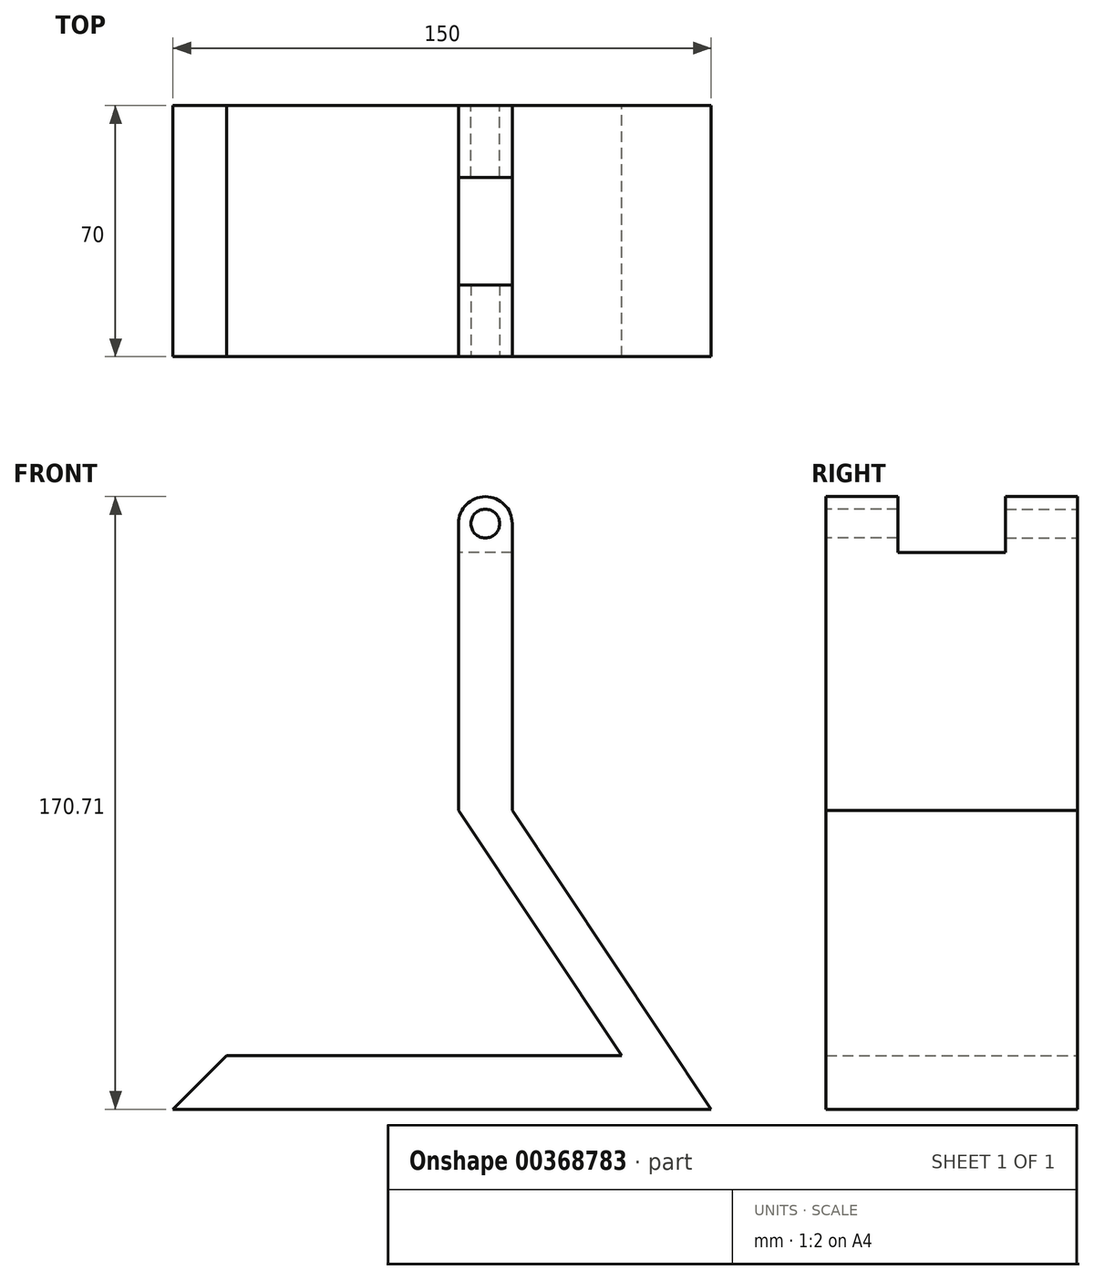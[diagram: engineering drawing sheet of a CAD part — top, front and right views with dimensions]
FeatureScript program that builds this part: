
annotation { "Feature Type Name" : "Feature", "Feature Type Description" : "" }
export const myFeature = defineFeature(function(context is Context, id is Id, definition is map)
    precondition{}
    {
        {
            var Q0;
            Q0=qCreatedBy(makeId("Top.planeOp"),FACE);
            var sketch = newSketch(context, id + "F0", { "sketchPlane" : qUnion([Q0])});
            skLineSegment(sketch, "E0.bottom", {"start": v(-62.5, 35) * mm, "end": v(62.5, 35) * mm});
            skLineSegment(sketch, "E0.top", {"start": v(-62.5, -35) * mm, "end": v(62.5, -35) * mm});
            skLineSegment(sketch, "E0.left", {"start": v(-62.5, 35) * mm, "end": v(-62.5, -35) * mm});
            skLineSegment(sketch, "E0.right", {"start": v(62.5, 35) * mm, "end": v(62.5, -35) * mm});
            skPoint(sketch, "E0.middle", {"position": v(0, 0) * mm});
            skSolve(sketch);
        }
        {
            var Q0;
            Q0 = qSketchRegion(id + "F0", true);
            extrude(context, id + "F1", {"entities" : qUnion([Q0]), "depth" : 15 * mm});
        }
        {
            var Q0;
            Q0=makeQuery(id+"F1.opExtrude","SWEPT_FACE",FACE,{"disambiguationData":[OSD([sQuery(id+"F0.wireOp",EDGE,"E0.top")])]});
            var sketch = newSketch(context, id + "F2", { "sketchPlane" : qUnion([Q0])});
            skLineSegment(sketch, "E1", {"start": v(62.5, 0) * mm, "end": v(72.5, 0) * mm});
            skLineSegment(sketch, "E2", {"start": v(72.5, 0) * mm, "end": v(62.5, 15) * mm});
            skSolve(sketch);
        }
        {
            var Q0;
            Q0=makeQuery(id+"F2.imprint","IMPRINT",FACE,{"disambiguationData":[TD([[makeQuery(id+"F2.imprint","IMPRINT",EDGE,{"derivedFrom":sQuery(id+"F2.wireOp",EDGE,"E1")}),1.0]])]});
            extrude(context, id + "F3", {"entities" : qUnion([Q0]), "operationType" : NewBodyOperationType.ADD, "oppositeDirection" : true, "depth" : 70 * mm});
        }
        {
            var Q0;
            {var subQ0=sQuery(id+"F0.wireOp",EDGE,"E0.top");Q0=makeQuery(id+"F3.boolean.opBoolean","MERGE",FACE,{"derivedFrom":[makeQuery(id+"F1.opExtrude","SWEPT_FACE",FACE,{"disambiguationData":[OSD([subQ0])]}),makeQuery(id+"F3.opExtrude","CAP_FACE",FACE,{"disambiguationData":[OSD([subQ0,sQuery(id+"F0.wireOp",EDGE,"E0.right"),sQuery(id+"F2.wireOp",EDGE,"E1"),sQuery(id+"F2.wireOp",EDGE,"E2")])],"isStart":true})]});}
            var sketch = newSketch(context, id + "F4", { "sketchPlane" : qUnion([Q0])});
            skLineSegment(sketch, "E3", {"start": v(-62.5, 0) * mm, "end": v(-77.5, 0) * mm});
            skLineSegment(sketch, "E4", {"start": v(-77.5, 0) * mm, "end": v(-62.5, 15) * mm});
            skSolve(sketch);
        }
        {
            var Q0;
            Q0=makeQuery(id+"F4.imprint","IMPRINT",FACE,{"disambiguationData":[TD([[makeQuery(id+"F4.imprint","IMPRINT",EDGE,{"derivedFrom":sQuery(id+"F4.wireOp",EDGE,"E3")}),-1.0]])]});
            extrude(context, id + "F5", {"entities" : qUnion([Q0]), "operationType" : NewBodyOperationType.ADD, "oppositeDirection" : true, "depth" : 70 * mm});
        }
        {
            var Q0;
            {var subQ0=sQuery(id+"F0.wireOp",EDGE,"E0.top");Q0=makeQuery(id+"F5.boolean.opBoolean","MERGE",FACE,{"derivedFrom":[makeQuery(id+"F3.boolean.opBoolean","MERGE",FACE,{"derivedFrom":[makeQuery(id+"F1.opExtrude","SWEPT_FACE",FACE,{"disambiguationData":[OSD([sQuery(id+"F0.wireOp",EDGE,"E0.bottom")])]}),makeQuery(id+"F3.opExtrude","CAP_FACE",FACE,{"disambiguationData":[OSD([subQ0,sQuery(id+"F0.wireOp",EDGE,"E0.right"),sQuery(id+"F2.wireOp",EDGE,"E1"),sQuery(id+"F2.wireOp",EDGE,"E2")])],"isStart":false})]}),makeQuery(id+"F5.opExtrude","CAP_FACE",FACE,{"disambiguationData":[OSD([subQ0,sQuery(id+"F0.wireOp",EDGE,"E0.left"),sQuery(id+"F4.wireOp",EDGE,"E3"),sQuery(id+"F4.wireOp",EDGE,"E4")])],"isStart":false})]});}
            var sketch = newSketch(context, id + "F6", { "sketchPlane" : qUnion([Q0])});
            skLineSegment(sketch, "E5", {"start": v(-72.5, 0) * mm, "end": v(-17.03, 83.2) * mm});
            skLineSegment(sketch, "E6", {"start": v(-17.03, 83.2) * mm, "end": v(-2.03, 83.2) * mm});
            skLineSegment(sketch, "E7", {"start": v(-2.03, 83.2) * mm, "end": v(-57.5, 0) * mm});
            skSolve(sketch);
        }
        {
            var Q0;
            {var subQ3=sQuery(id+"F6.wireOp",EDGE,"E6");Q0=makeQuery(id+"F6.imprint","IMPRINT",FACE,{"disambiguationData":[TD([[makeQuery(id+"F6.imprint","IMPRINT",EDGE,{"derivedFrom":subQ3}),-1.0]])]});}
            extrude(context, id + "F7", {"entities" : qUnion([Q0]), "operationType" : NewBodyOperationType.ADD, "oppositeDirection" : true, "depth" : 70 * mm});
        }
        {
            var Q0;
            {var subQ0=sQuery(id+"F0.wireOp",EDGE,"E0.top");Q0=makeQuery(id+"F7.boolean.opBoolean","MERGE",FACE,{"derivedFrom":[makeQuery(id+"F5.boolean.opBoolean","MERGE",FACE,{"derivedFrom":[makeQuery(id+"F3.boolean.opBoolean","MERGE",FACE,{"derivedFrom":[makeQuery(id+"F1.opExtrude","SWEPT_FACE",FACE,{"disambiguationData":[OSD([subQ0])]}),makeQuery(id+"F3.opExtrude","CAP_FACE",FACE,{"disambiguationData":[OSD([subQ0,sQuery(id+"F0.wireOp",EDGE,"E0.right"),sQuery(id+"F2.wireOp",EDGE,"E1"),sQuery(id+"F2.wireOp",EDGE,"E2")])],"isStart":true})]}),makeQuery(id+"F5.opExtrude","CAP_FACE",FACE,{"disambiguationData":[OSD([subQ0,sQuery(id+"F0.wireOp",EDGE,"E0.left"),sQuery(id+"F4.wireOp",EDGE,"E3"),sQuery(id+"F4.wireOp",EDGE,"E4")])],"isStart":true})]}),makeQuery(id+"F7.opExtrude","CAP_FACE",FACE,{"disambiguationData":[OSD([sQuery(id+"F0.wireOp",EDGE,"E0.bottom"),sQuery(id+"F6.wireOp",EDGE,"E5"),sQuery(id+"F6.wireOp",EDGE,"E6"),sQuery(id+"F6.wireOp",EDGE,"E7")])],"isStart":false})]});}
            var sketch = newSketch(context, id + "F8", { "sketchPlane" : qUnion([Q0])});
            skLineSegment(sketch, "E8.bottom", {"start": v(2.03, 83.2) * mm, "end": v(17.03, 83.2) * mm});
            skLineSegment(sketch, "E8.top", {"start": v(2.03, 163.2) * mm, "end": v(17.03, 163.2) * mm});
            skLineSegment(sketch, "E8.left", {"start": v(2.03, 83.2) * mm, "end": v(2.03, 163.2) * mm});
            skLineSegment(sketch, "E8.right", {"start": v(17.03, 83.2) * mm, "end": v(17.03, 163.2) * mm});
            skCircle(sketch, "E9", {"center": v(9.53, 163.2) * mm, "radius": 7.5 * mm});
            skCircle(sketch, "E10", {"center": v(9.53, 163.2) * mm, "radius": 4 * mm});
            skSolve(sketch);
        }
        {
            var Q0;
            Q0 = qSketchRegion(id + "F8", true);
            extrude(context, id + "F9", {"entities" : qUnion([Q0]), "operationType" : NewBodyOperationType.ADD, "oppositeDirection" : true, "depth" : 20 * mm});
        }
        {
            var Q0;
            {var subQ0=sQuery(id+"F0.wireOp",EDGE,"E0.bottom");var subQ1=sQuery(id+"F0.wireOp",EDGE,"E0.top");Q0=makeQuery(id+"F7.boolean.opBoolean","MERGE",FACE,{"derivedFrom":[makeQuery(id+"F5.boolean.opBoolean","MERGE",FACE,{"derivedFrom":[makeQuery(id+"F3.boolean.opBoolean","MERGE",FACE,{"derivedFrom":[makeQuery(id+"F1.opExtrude","SWEPT_FACE",FACE,{"disambiguationData":[OSD([subQ0])]}),makeQuery(id+"F3.opExtrude","CAP_FACE",FACE,{"disambiguationData":[OSD([subQ1,sQuery(id+"F0.wireOp",EDGE,"E0.right"),sQuery(id+"F2.wireOp",EDGE,"E1"),sQuery(id+"F2.wireOp",EDGE,"E2")])],"isStart":false})]}),makeQuery(id+"F5.opExtrude","CAP_FACE",FACE,{"disambiguationData":[OSD([subQ1,sQuery(id+"F0.wireOp",EDGE,"E0.left"),sQuery(id+"F4.wireOp",EDGE,"E3"),sQuery(id+"F4.wireOp",EDGE,"E4")])],"isStart":false})]}),makeQuery(id+"F7.opExtrude","CAP_FACE",FACE,{"disambiguationData":[OSD([subQ0,sQuery(id+"F6.wireOp",EDGE,"E5"),sQuery(id+"F6.wireOp",EDGE,"E6"),sQuery(id+"F6.wireOp",EDGE,"E7")])],"isStart":true})]});}
            var sketch = newSketch(context, id + "F10", { "sketchPlane" : qUnion([Q0])});
            skLineSegment(sketch, "E11.bottom", {"start": v(-17.03, 83.2) * mm, "end": v(-2.03, 83.2) * mm});
            skLineSegment(sketch, "E11.top", {"start": v(-17.03, 163.2) * mm, "end": v(-2.03, 163.2) * mm});
            skLineSegment(sketch, "E11.left", {"start": v(-17.03, 83.2) * mm, "end": v(-17.03, 163.2) * mm});
            skLineSegment(sketch, "E11.right", {"start": v(-2.03, 83.2) * mm, "end": v(-2.03, 163.2) * mm});
            skCircle(sketch, "E12", {"center": v(-9.53, 163.2) * mm, "radius": 7.5 * mm});
            skCircle(sketch, "E13", {"center": v(-9.53, 163.2) * mm, "radius": 4 * mm});
            skSolve(sketch);
        }
        {
            var Q0;
            Q0 = qSketchRegion(id + "F10", true);
            extrude(context, id + "F11", {"entities" : qUnion([Q0]), "operationType" : NewBodyOperationType.ADD, "oppositeDirection" : true, "depth" : 20 * mm});
        }
        {
            var Q0;
            Q0=makeQuery(id+"F7.opExtrude","SWEPT_FACE",FACE,{"disambiguationData":[OSD([sQuery(id+"F6.wireOp",EDGE,"E6")])]});
            var sketch = newSketch(context, id + "F12", { "sketchPlane" : qUnion([Q0])});
            skLineSegment(sketch, "E14.bottom", {"start": v(17.03, 15) * mm, "end": v(2.03, 15) * mm});
            skLineSegment(sketch, "E14.top", {"start": v(17.03, -15) * mm, "end": v(2.03, -15) * mm});
            skLineSegment(sketch, "E14.left", {"start": v(17.03, 15) * mm, "end": v(17.03, -15) * mm});
            skLineSegment(sketch, "E14.right", {"start": v(2.03, 15) * mm, "end": v(2.03, -15) * mm});
            skSolve(sketch);
        }
        {
            var Q0;
            Q0 = qSketchRegion(id + "F12", true);
            extrude(context, id + "F13", {"entities" : qUnion([Q0]), "operationType" : NewBodyOperationType.ADD, "depth" : 72 * mm});
        }
    });
